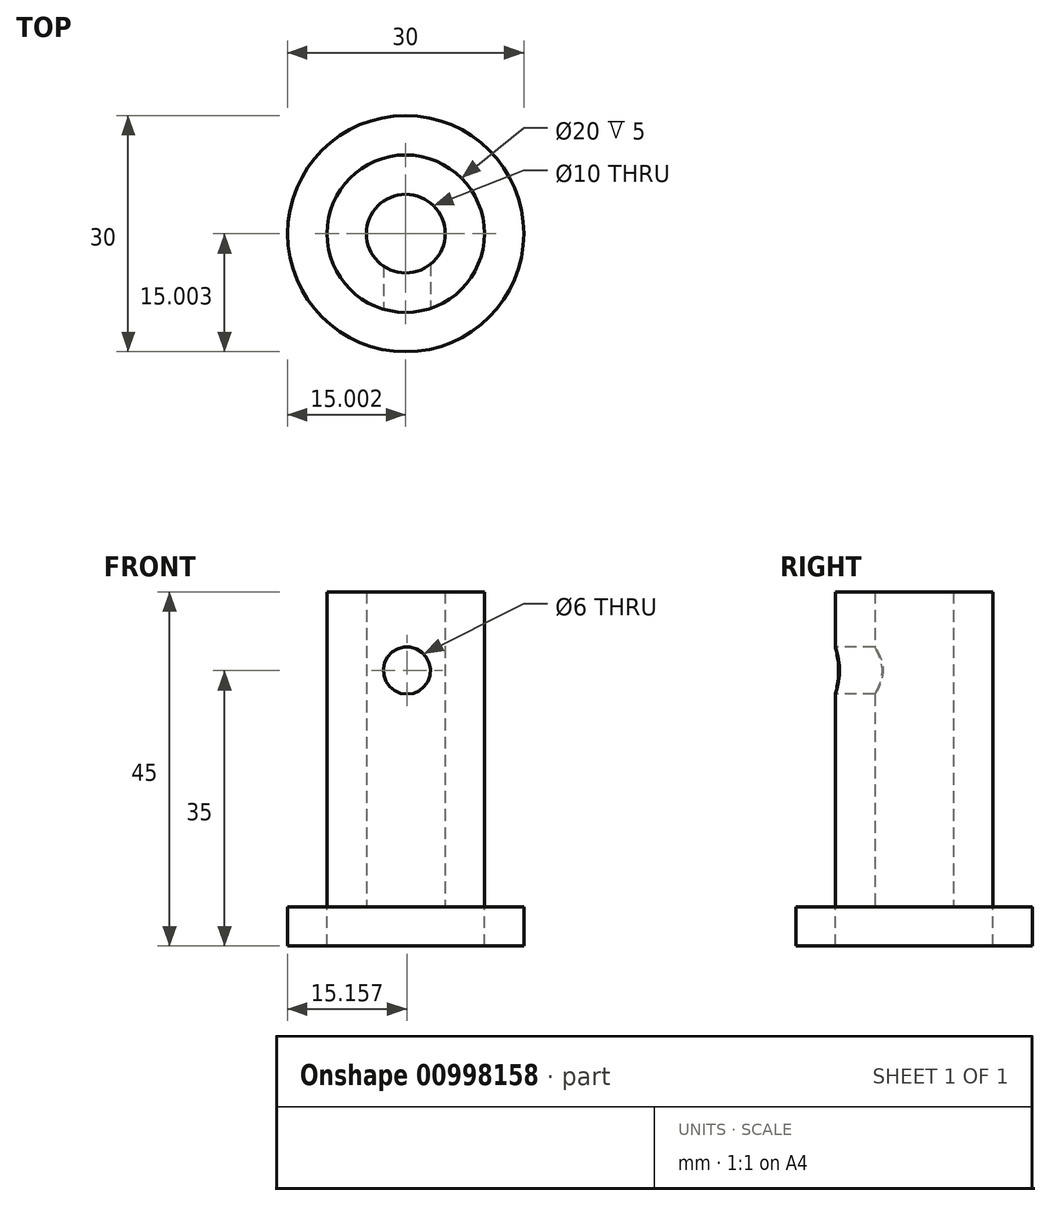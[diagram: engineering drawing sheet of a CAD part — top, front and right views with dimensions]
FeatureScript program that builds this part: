
annotation { "Feature Type Name" : "Feature", "Feature Type Description" : "" }
export const myFeature = defineFeature(function(context is Context, id is Id, definition is map)
    precondition{}
    {
        {
            var Q0;
            Q0=qCreatedBy(makeId("Top.planeOp"),FACE);
            var sketch = newSketch(context, id + "F0", { "sketchPlane" : qUnion([Q0])});
            skCircle(sketch, "E0", {"center": v(96.3, 20.1) * mm, "radius": 10 * mm});
            skCircle(sketch, "E1", {"center": v(96.3, 20.1) * mm, "radius": 5 * mm});
            skSolve(sketch);
        }
        {
            var Q0;
            Q0=makeQuery(id+"F0.imprint","IMPRINT",FACE,{"disambiguationData":[TD([[makeQuery(id+"F0.imprint","IMPRINT",EDGE,{"derivedFrom":sQuery(id+"F0.wireOp",EDGE,"E0")}),1.0]])]});
            extrude(context, id + "F1", {"entities" : qUnion([Q0]), "depth" : 40 * mm, "offsetDistance" : 25 * mm});
        }
        {
            var Q0;
            Q0=qCreatedBy(makeId("Front.planeOp"),FACE);
            var sketch = newSketch(context, id + "F2", { "sketchPlane" : qUnion([Q0])});
            skCircle(sketch, "E2", {"center": v(96.45, 30) * mm, "radius": 3 * mm});
            skSolve(sketch);
        }
        {
            var Q0;
            Q0=sQuery(id+"F2.wireOp",VERTEX,"E2.center");
            var Q1;
            Q1=makeQuery(id+"F1.opExtrude","SWEPT_BODY",BODY,{"disambiguationData":[OSD([sQuery(id+"F0.wireOp",EDGE,"E0"),sQuery(id+"F0.wireOp",EDGE,"E1")])]});
            hole(context, id + "F3", {"style" : HoleStyle.SIMPLE, "endStyle" : HoleEndStyle.BLIND, "holeDiameter" : 6 * mm, "majorDiameter" : 5 * mm, "holeDepth" : 12 * mm, "isTappedThrough" : true, "tappedDepth" : 12 * mm, "tapClearance" : 3, "locations" : qUnion([Q0]), "scope" : qUnion([Q1])});
        }
        {
            var Q0;
            Q0=makeQuery(id+"F1.opExtrude","CAP_FACE",FACE,{"disambiguationData":[OSD([sQuery(id+"F0.wireOp",EDGE,"E0"),sQuery(id+"F0.wireOp",EDGE,"E1")])],"isStart":true});
            var sketch = newSketch(context, id + "F4", { "sketchPlane" : qUnion([Q0])});
            skCircle(sketch, "E3", {"center": v(96.3, -20.1) * mm, "radius": 15 * mm});
            skSolve(sketch);
        }
        {
            var Q0;
            Q0=makeQuery(id+"F4.imprint","IMPRINT",FACE,{"disambiguationData":[TD([[makeQuery(id+"F4.imprint","IMPRINT",EDGE,{"derivedFrom":sQuery(id+"F4.wireOp",EDGE,"E3")}),1.0]])]});
            extrude(context, id + "F5", {"entities" : qUnion([Q0]), "depth" : 5 * mm, "offsetDistance" : 25 * mm});
        }
    });
